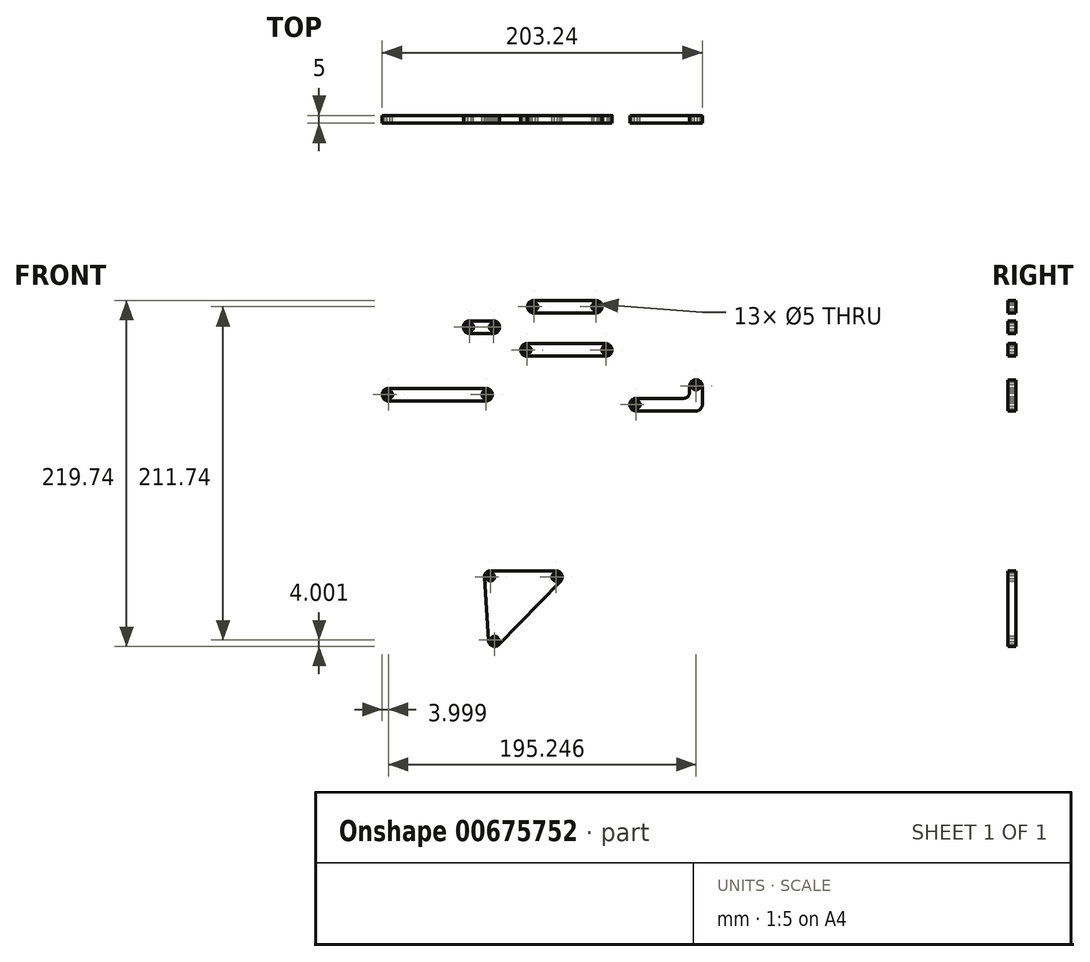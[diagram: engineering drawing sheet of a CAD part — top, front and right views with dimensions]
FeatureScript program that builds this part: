
annotation { "Feature Type Name" : "Feature", "Feature Type Description" : "" }
export const myFeature = defineFeature(function(context is Context, id is Id, definition is map)
    precondition{}
    {
        {
            var Q0;
            Q0=qCreatedBy(makeId("Front.planeOp"),FACE);
            var sketch = newSketch(context, id + "F0", { "sketchPlane" : qUnion([Q0])});
            skLineSegment(sketch, "E0.bottom", {"start": v(-7.5, 4) * mm, "end": v(7.5, 4) * mm});
            skLineSegment(sketch, "E0.top", {"start": v(-7.5, -4) * mm, "end": v(7.5, -4) * mm});
            skLineSegment(sketch, "E0.left", {"start": v(-7.5, 4) * mm, "end": v(-7.5, -4) * mm});
            skLineSegment(sketch, "E0.right", {"start": v(7.5, 4) * mm, "end": v(7.5, -4) * mm});
            skArc(sketch, "E1", {"start": v(7.5, -4) * mm, "mid": v(11.5, 0) * mm, "end": v(7.5, 4) * mm});
            skArc(sketch, "E2", {"start": v(-7.5, 4) * mm, "mid": v(-11.5, 0) * mm, "end": v(-7.5, -4) * mm});
            skCircle(sketch, "E3", {"center": v(-7.5, 0) * mm, "radius": 2.5 * mm});
            skCircle(sketch, "E4", {"center": v(7.5, 0) * mm, "radius": 2.5 * mm});
            skCircle(sketch, "E5", {"center": v(-7.5, 0) * mm, "radius": 1 * mm});
            skCircle(sketch, "E6", {"center": v(7.5, 0) * mm, "radius": 1 * mm});
            skLineSegment(sketch, "E7", {"start": v(-7.5, 0) * mm, "end": v(7.5, 0) * mm});
            skSolve(sketch);
        }
        {
            var Q0;
            {var subQ6=sQuery(id+"F0.wireOp",EDGE,"E0.bottom");Q0=makeQuery(id+"F0.imprint","IMPRINT",FACE,{"disambiguationData":[TD([[makeQuery(id+"F0.imprint","IMPRINT",EDGE,{"derivedFrom":subQ6}),-1.0]])]});}
            var Q1;
            {var subQ5=sQuery(id+"F0.wireOp",EDGE,"E0.top");Q1=makeQuery(id+"F0.imprint","IMPRINT",FACE,{"disambiguationData":[TD([[makeQuery(id+"F0.imprint","IMPRINT",EDGE,{"derivedFrom":subQ5}),1.0]])]});}
            var Q2;
            {var subQ0=sQuery(id+"F0.wireOp",EDGE,"E2");Q2=makeQuery(id+"F0.imprint","IMPRINT",FACE,{"disambiguationData":[TD([[makeQuery(id+"F0.imprint","IMPRINT",EDGE,{"derivedFrom":subQ0}),1.0]])]});}
            var Q3;
            {var subQ0=sQuery(id+"F0.wireOp",EDGE,"E7");var subQ1=sQuery(id+"F0.wireOp",EDGE,"E0.left");var subQ2=makeQuery(id+"F0.imprint","INTERSECT",VERTEX,{"derivedFrom":[subQ1,subQ0]});Q3=makeQuery(id+"F0.imprint","IMPRINT",FACE,{"disambiguationData":[TD([[makeQuery(id+"F0.imprint","IMPRINT",EDGE,{"disambiguationData":[TD([[subQ2,1.0]])],"derivedFrom":subQ1}),1.0]])]});}
            var Q4;
            {var subQ0=sQuery(id+"F0.wireOp",EDGE,"E7");var subQ1=sQuery(id+"F0.wireOp",EDGE,"E0.left");var subQ2=makeQuery(id+"F0.imprint","INTERSECT",VERTEX,{"derivedFrom":[subQ1,subQ0]});Q4=makeQuery(id+"F0.imprint","IMPRINT",FACE,{"disambiguationData":[TD([[makeQuery(id+"F0.imprint","IMPRINT",EDGE,{"disambiguationData":[TD([[subQ2,-1.0]])],"derivedFrom":subQ1}),1.0]])]});}
            var Q5;
            {var subQ0=sQuery(id+"F0.wireOp",EDGE,"E0.left");var subQ1=makeQuery(id+"F0.imprint","INTERSECT",VERTEX,{"derivedFrom":[subQ0,sQuery(id+"F0.wireOp",EDGE,"E7")]});Q5=makeQuery(id+"F0.imprint","IMPRINT",FACE,{"disambiguationData":[TD([[makeQuery(id+"F0.imprint","IMPRINT",EDGE,{"disambiguationData":[TD([[subQ1,1.0]])],"derivedFrom":subQ0}),-1.0]])]});}
            var Q6;
            {var subQ0=sQuery(id+"F0.wireOp",EDGE,"E0.right");var subQ1=makeQuery(id+"F0.imprint","INTERSECT",VERTEX,{"derivedFrom":[subQ0,sQuery(id+"F0.wireOp",EDGE,"E7")]});Q6=makeQuery(id+"F0.imprint","IMPRINT",FACE,{"disambiguationData":[TD([[makeQuery(id+"F0.imprint","IMPRINT",EDGE,{"disambiguationData":[TD([[subQ1,1.0]])],"derivedFrom":subQ0}),1.0]])]});}
            var Q7;
            {var subQ0=sQuery(id+"F0.wireOp",EDGE,"E7");var subQ1=sQuery(id+"F0.wireOp",EDGE,"E0.right");var subQ2=makeQuery(id+"F0.imprint","INTERSECT",VERTEX,{"derivedFrom":[subQ1,subQ0]});Q7=makeQuery(id+"F0.imprint","IMPRINT",FACE,{"disambiguationData":[TD([[makeQuery(id+"F0.imprint","IMPRINT",EDGE,{"disambiguationData":[TD([[subQ2,1.0]])],"derivedFrom":subQ1}),-1.0]])]});}
            var Q8;
            {var subQ0=sQuery(id+"F0.wireOp",EDGE,"E7");var subQ1=sQuery(id+"F0.wireOp",EDGE,"E0.right");var subQ2=makeQuery(id+"F0.imprint","INTERSECT",VERTEX,{"derivedFrom":[subQ1,subQ0]});Q8=makeQuery(id+"F0.imprint","IMPRINT",FACE,{"disambiguationData":[TD([[makeQuery(id+"F0.imprint","IMPRINT",EDGE,{"disambiguationData":[TD([[subQ2,-1.0]])],"derivedFrom":subQ1}),-1.0]])]});}
            var Q9;
            {var subQ0=sQuery(id+"F0.wireOp",EDGE,"E1");Q9=makeQuery(id+"F0.imprint","IMPRINT",FACE,{"disambiguationData":[TD([[makeQuery(id+"F0.imprint","IMPRINT",EDGE,{"derivedFrom":subQ0}),1.0]])]});}
            extrude(context, id + "F1", {"entities" : qUnion([Q0, Q1, Q2, Q3, Q4, Q5, Q6, Q7, Q8, Q9]), "endBound" : BoundingType.SYMMETRIC, "depth" : 5 * mm, "offsetDistance" : 25 * mm});
        }
        {
            var Q0;
            Q0=qCreatedBy(makeId("Front.planeOp"),FACE);
            var sketch = newSketch(context, id + "F2", { "sketchPlane" : qUnion([Q0])});
            skLineSegment(sketch, "E8.bottom", {"start": v(33.28, 16.95) * mm, "end": v(72.58, 16.95) * mm});
            skLineSegment(sketch, "E8.top", {"start": v(33.28, 8.95) * mm, "end": v(72.58, 8.95) * mm});
            skLineSegment(sketch, "E8.left", {"start": v(33.28, 16.95) * mm, "end": v(33.28, 8.95) * mm});
            skLineSegment(sketch, "E8.right", {"start": v(72.58, 16.95) * mm, "end": v(72.58, 8.95) * mm});
            skArc(sketch, "E9", {"start": v(33.28, 16.95) * mm, "mid": v(29.28, 12.95) * mm, "end": v(33.28, 8.95) * mm});
            skArc(sketch, "E10", {"start": v(72.58, 8.95) * mm, "mid": v(76.58, 12.95) * mm, "end": v(72.58, 16.95) * mm});
            skCircle(sketch, "E11", {"center": v(33.28, 12.95) * mm, "radius": 2.5 * mm});
            skCircle(sketch, "E12", {"center": v(33.28, 12.95) * mm, "radius": 1 * mm});
            skCircle(sketch, "E13", {"center": v(72.58, 12.95) * mm, "radius": 2.5 * mm});
            skCircle(sketch, "E14", {"center": v(72.58, 12.95) * mm, "radius": 1 * mm});
            skSolve(sketch);
        }
        {
            var Q0;
            {var subQ2=sQuery(id+"F2.wireOp",EDGE,"E8.bottom");Q0=makeQuery(id+"F2.imprint","IMPRINT",FACE,{"disambiguationData":[TD([[makeQuery(id+"F2.imprint","IMPRINT",EDGE,{"derivedFrom":subQ2}),-1.0]])]});}
            var Q1;
            {var subQ0=sQuery(id+"F2.wireOp",EDGE,"E9");Q1=makeQuery(id+"F2.imprint","IMPRINT",FACE,{"disambiguationData":[TD([[makeQuery(id+"F2.imprint","IMPRINT",EDGE,{"derivedFrom":subQ0}),1.0]])]});}
            var Q2;
            {var subQ0=sQuery(id+"F2.wireOp",EDGE,"E10");Q2=makeQuery(id+"F2.imprint","IMPRINT",FACE,{"disambiguationData":[TD([[makeQuery(id+"F2.imprint","IMPRINT",EDGE,{"derivedFrom":subQ0}),1.0]])]});}
            var Q3;
            {var subQ0=sQuery(id+"F2.wireOp",EDGE,"E14");var subQ1=sQuery(id+"F2.wireOp",EDGE,"E8.right");var subQ2=makeQuery(id+"F2.imprint","INTERSECT",VERTEX,{"disambiguationData":[OD(0.0)],"derivedFrom":[subQ1,subQ0]});Q3=makeQuery(id+"F2.imprint","IMPRINT",FACE,{"disambiguationData":[TD([[makeQuery(id+"F2.imprint","IMPRINT",EDGE,{"disambiguationData":[TD([[subQ2,-1.0]])],"derivedFrom":subQ1}),1.0]])]});}
            var Q4;
            {var subQ0=sQuery(id+"F2.wireOp",EDGE,"E14");var subQ1=sQuery(id+"F2.wireOp",EDGE,"E8.right");var subQ2=makeQuery(id+"F2.imprint","INTERSECT",VERTEX,{"disambiguationData":[OD(0.0)],"derivedFrom":[subQ1,subQ0]});Q4=makeQuery(id+"F2.imprint","IMPRINT",FACE,{"disambiguationData":[TD([[makeQuery(id+"F2.imprint","IMPRINT",EDGE,{"disambiguationData":[TD([[subQ2,-1.0]])],"derivedFrom":subQ1}),-1.0]])]});}
            var Q5;
            {var subQ0=sQuery(id+"F2.wireOp",EDGE,"E12");var subQ1=sQuery(id+"F2.wireOp",EDGE,"E8.left");var subQ2=makeQuery(id+"F2.imprint","INTERSECT",VERTEX,{"disambiguationData":[OD(0.0)],"derivedFrom":[subQ1,subQ0]});Q5=makeQuery(id+"F2.imprint","IMPRINT",FACE,{"disambiguationData":[TD([[makeQuery(id+"F2.imprint","IMPRINT",EDGE,{"disambiguationData":[TD([[subQ2,-1.0]])],"derivedFrom":subQ1}),1.0]])]});}
            var Q6;
            {var subQ0=sQuery(id+"F2.wireOp",EDGE,"E12");var subQ1=sQuery(id+"F2.wireOp",EDGE,"E8.left");var subQ2=makeQuery(id+"F2.imprint","INTERSECT",VERTEX,{"disambiguationData":[OD(0.0)],"derivedFrom":[subQ1,subQ0]});Q6=makeQuery(id+"F2.imprint","IMPRINT",FACE,{"disambiguationData":[TD([[makeQuery(id+"F2.imprint","IMPRINT",EDGE,{"disambiguationData":[TD([[subQ2,-1.0]])],"derivedFrom":subQ1}),-1.0]])]});}
            extrude(context, id + "F3", {"entities" : qUnion([Q0, Q1, Q2, Q3, Q4, Q5, Q6]), "endBound" : BoundingType.SYMMETRIC, "depth" : 5 * mm, "offsetDistance" : 25 * mm});
        }
        {
            var Q0;
            Q0=qCreatedBy(makeId("Front.planeOp"),FACE);
            var sketch = newSketch(context, id + "F4", { "sketchPlane" : qUnion([Q0])});
            skLineSegment(sketch, "E15.bottom", {"start": v(28.9, -10.5) * mm, "end": v(78.9, -10.5) * mm});
            skLineSegment(sketch, "E15.top", {"start": v(28.9, -18.5) * mm, "end": v(78.9, -18.5) * mm});
            skLineSegment(sketch, "E15.left", {"start": v(28.9, -10.5) * mm, "end": v(28.9, -18.5) * mm});
            skLineSegment(sketch, "E15.right", {"start": v(78.9, -10.5) * mm, "end": v(78.9, -18.5) * mm});
            skArc(sketch, "E16", {"start": v(28.9, -10.5) * mm, "mid": v(24.9, -14.5) * mm, "end": v(28.9, -18.5) * mm});
            skArc(sketch, "E17", {"start": v(78.9, -18.5) * mm, "mid": v(82.9, -14.5) * mm, "end": v(78.9, -10.5) * mm});
            skCircle(sketch, "E18", {"center": v(28.9, -14.5) * mm, "radius": 2.5 * mm});
            skCircle(sketch, "E19", {"center": v(28.9, -14.5) * mm, "radius": 1 * mm});
            skCircle(sketch, "E20", {"center": v(78.9, -14.5) * mm, "radius": 2.5 * mm});
            skCircle(sketch, "E21", {"center": v(78.9, -14.5) * mm, "radius": 1 * mm});
            skSolve(sketch);
        }
        {
            var Q0;
            {var subQ2=sQuery(id+"F4.wireOp",EDGE,"E15.bottom");Q0=makeQuery(id+"F4.imprint","IMPRINT",FACE,{"disambiguationData":[TD([[makeQuery(id+"F4.imprint","IMPRINT",EDGE,{"derivedFrom":subQ2}),-1.0]])]});}
            var Q1;
            {var subQ0=sQuery(id+"F4.wireOp",EDGE,"E16");Q1=makeQuery(id+"F4.imprint","IMPRINT",FACE,{"disambiguationData":[TD([[makeQuery(id+"F4.imprint","IMPRINT",EDGE,{"derivedFrom":subQ0}),1.0]])]});}
            var Q2;
            {var subQ0=sQuery(id+"F4.wireOp",EDGE,"E17");Q2=makeQuery(id+"F4.imprint","IMPRINT",FACE,{"disambiguationData":[TD([[makeQuery(id+"F4.imprint","IMPRINT",EDGE,{"derivedFrom":subQ0}),1.0]])]});}
            var Q3;
            {var subQ0=sQuery(id+"F4.wireOp",EDGE,"E21");var subQ1=sQuery(id+"F4.wireOp",EDGE,"E15.right");var subQ2=makeQuery(id+"F4.imprint","INTERSECT",VERTEX,{"disambiguationData":[OD(0.0)],"derivedFrom":[subQ1,subQ0]});Q3=makeQuery(id+"F4.imprint","IMPRINT",FACE,{"disambiguationData":[TD([[makeQuery(id+"F4.imprint","IMPRINT",EDGE,{"disambiguationData":[TD([[subQ2,-1.0]])],"derivedFrom":subQ1}),1.0]])]});}
            var Q4;
            {var subQ0=sQuery(id+"F4.wireOp",EDGE,"E21");var subQ1=sQuery(id+"F4.wireOp",EDGE,"E15.right");var subQ2=makeQuery(id+"F4.imprint","INTERSECT",VERTEX,{"disambiguationData":[OD(0.0)],"derivedFrom":[subQ1,subQ0]});Q4=makeQuery(id+"F4.imprint","IMPRINT",FACE,{"disambiguationData":[TD([[makeQuery(id+"F4.imprint","IMPRINT",EDGE,{"disambiguationData":[TD([[subQ2,-1.0]])],"derivedFrom":subQ1}),-1.0]])]});}
            var Q5;
            {var subQ0=sQuery(id+"F4.wireOp",EDGE,"E19");var subQ1=sQuery(id+"F4.wireOp",EDGE,"E15.left");var subQ2=makeQuery(id+"F4.imprint","INTERSECT",VERTEX,{"disambiguationData":[OD(0.0)],"derivedFrom":[subQ1,subQ0]});Q5=makeQuery(id+"F4.imprint","IMPRINT",FACE,{"disambiguationData":[TD([[makeQuery(id+"F4.imprint","IMPRINT",EDGE,{"disambiguationData":[TD([[subQ2,-1.0]])],"derivedFrom":subQ1}),1.0]])]});}
            var Q6;
            {var subQ0=sQuery(id+"F4.wireOp",EDGE,"E19");var subQ1=sQuery(id+"F4.wireOp",EDGE,"E15.left");var subQ2=makeQuery(id+"F4.imprint","INTERSECT",VERTEX,{"disambiguationData":[OD(0.0)],"derivedFrom":[subQ1,subQ0]});Q6=makeQuery(id+"F4.imprint","IMPRINT",FACE,{"disambiguationData":[TD([[makeQuery(id+"F4.imprint","IMPRINT",EDGE,{"disambiguationData":[TD([[subQ2,-1.0]])],"derivedFrom":subQ1}),-1.0]])]});}
            extrude(context, id + "F5", {"entities" : qUnion([Q0, Q1, Q2, Q3, Q4, Q5, Q6]), "endBound" : BoundingType.SYMMETRIC, "depth" : 5 * mm, "offsetDistance" : 25 * mm});
        }
        {
            var Q0;
            Q0=qCreatedBy(makeId("Front.planeOp"),FACE);
            var sketch = newSketch(context, id + "F6", { "sketchPlane" : qUnion([Q0])});
            skLineSegment(sketch, "E22.bottom", {"start": v(-59.03, -46.94) * mm, "end": v(2.87, -46.94) * mm});
            skLineSegment(sketch, "E22.top", {"start": v(-59.03, -38.94) * mm, "end": v(2.87, -38.94) * mm});
            skLineSegment(sketch, "E22.left", {"start": v(-59.03, -46.94) * mm, "end": v(-59.03, -38.94) * mm});
            skLineSegment(sketch, "E22.right", {"start": v(2.87, -46.94) * mm, "end": v(2.87, -38.94) * mm});
            skArc(sketch, "E23", {"start": v(-59.03, -38.94) * mm, "mid": v(-63.03, -42.94) * mm, "end": v(-59.03, -46.94) * mm});
            skArc(sketch, "E24", {"start": v(2.87, -46.94) * mm, "mid": v(6.87, -42.94) * mm, "end": v(2.87, -38.94) * mm});
            skCircle(sketch, "E25", {"center": v(-59.03, -42.94) * mm, "radius": 2.5 * mm});
            skCircle(sketch, "E26", {"center": v(2.87, -42.94) * mm, "radius": 2.5 * mm});
            skCircle(sketch, "E27", {"center": v(2.87, -42.94) * mm, "radius": 1 * mm});
            skCircle(sketch, "E28", {"center": v(-59.03, -42.94) * mm, "radius": 1 * mm});
            skSolve(sketch);
        }
        {
            var Q0;
            {var subQ2=sQuery(id+"F6.wireOp",EDGE,"E22.bottom");Q0=makeQuery(id+"F6.imprint","IMPRINT",FACE,{"disambiguationData":[TD([[makeQuery(id+"F6.imprint","IMPRINT",EDGE,{"derivedFrom":subQ2}),1.0]])]});}
            var Q1;
            {var subQ0=sQuery(id+"F6.wireOp",EDGE,"E23");Q1=makeQuery(id+"F6.imprint","IMPRINT",FACE,{"disambiguationData":[TD([[makeQuery(id+"F6.imprint","IMPRINT",EDGE,{"derivedFrom":subQ0}),1.0]])]});}
            var Q2;
            {var subQ0=sQuery(id+"F6.wireOp",EDGE,"E28");var subQ1=sQuery(id+"F6.wireOp",EDGE,"E22.left");var subQ2=makeQuery(id+"F6.imprint","INTERSECT",VERTEX,{"disambiguationData":[OD(0.0)],"derivedFrom":[subQ1,subQ0]});Q2=makeQuery(id+"F6.imprint","IMPRINT",FACE,{"disambiguationData":[TD([[makeQuery(id+"F6.imprint","IMPRINT",EDGE,{"disambiguationData":[TD([[subQ2,-1.0]])],"derivedFrom":subQ1}),-1.0]])]});}
            var Q3;
            {var subQ0=sQuery(id+"F6.wireOp",EDGE,"E28");var subQ1=sQuery(id+"F6.wireOp",EDGE,"E22.left");var subQ2=makeQuery(id+"F6.imprint","INTERSECT",VERTEX,{"disambiguationData":[OD(0.0)],"derivedFrom":[subQ1,subQ0]});Q3=makeQuery(id+"F6.imprint","IMPRINT",FACE,{"disambiguationData":[TD([[makeQuery(id+"F6.imprint","IMPRINT",EDGE,{"disambiguationData":[TD([[subQ2,-1.0]])],"derivedFrom":subQ1}),1.0]])]});}
            var Q4;
            {var subQ0=sQuery(id+"F6.wireOp",EDGE,"E24");Q4=makeQuery(id+"F6.imprint","IMPRINT",FACE,{"disambiguationData":[TD([[makeQuery(id+"F6.imprint","IMPRINT",EDGE,{"derivedFrom":subQ0}),1.0]])]});}
            var Q5;
            {var subQ0=sQuery(id+"F6.wireOp",EDGE,"E27");var subQ1=sQuery(id+"F6.wireOp",EDGE,"E22.right");var subQ2=makeQuery(id+"F6.imprint","INTERSECT",VERTEX,{"disambiguationData":[OD(0.0)],"derivedFrom":[subQ1,subQ0]});Q5=makeQuery(id+"F6.imprint","IMPRINT",FACE,{"disambiguationData":[TD([[makeQuery(id+"F6.imprint","IMPRINT",EDGE,{"disambiguationData":[TD([[subQ2,-1.0]])],"derivedFrom":subQ1}),-1.0]])]});}
            var Q6;
            {var subQ0=sQuery(id+"F6.wireOp",EDGE,"E27");var subQ1=sQuery(id+"F6.wireOp",EDGE,"E22.right");var subQ2=makeQuery(id+"F6.imprint","INTERSECT",VERTEX,{"disambiguationData":[OD(0.0)],"derivedFrom":[subQ1,subQ0]});Q6=makeQuery(id+"F6.imprint","IMPRINT",FACE,{"disambiguationData":[TD([[makeQuery(id+"F6.imprint","IMPRINT",EDGE,{"disambiguationData":[TD([[subQ2,-1.0]])],"derivedFrom":subQ1}),1.0]])]});}
            extrude(context, id + "F7", {"entities" : qUnion([Q0, Q1, Q2, Q3, Q4, Q5, Q6]), "endBound" : BoundingType.SYMMETRIC, "depth" : 5 * mm, "offsetDistance" : 25 * mm});
        }
        {
            var Q0;
            Q0=qCreatedBy(makeId("Front.planeOp"),FACE);
            var sketch = newSketch(context, id + "F8", { "sketchPlane" : qUnion([Q0])});
            skLineSegment(sketch, "E29.bottom", {"start": v(98.21, -45.24) * mm, "end": v(128.21, -45.24) * mm});
            skLineSegment(sketch, "E29.top", {"start": v(98.21, -53.24) * mm, "end": v(136.21, -53.24) * mm});
            skLineSegment(sketch, "E29.left", {"start": v(98.21, -45.24) * mm, "end": v(98.21, -53.24) * mm});
            skLineSegment(sketch, "E29.right", {"start": v(140.21, -45.24) * mm, "end": v(140.21, -49.24) * mm});
            skArc(sketch, "E30", {"start": v(98.21, -45.24) * mm, "mid": v(94.21, -49.24) * mm, "end": v(98.21, -53.24) * mm});
            skLineSegment(sketch, "E31.top", {"start": v(140.21, -37.44) * mm, "end": v(132.21, -37.44) * mm});
            skLineSegment(sketch, "E31.left", {"start": v(140.21, -45.24) * mm, "end": v(140.21, -37.44) * mm});
            skLineSegment(sketch, "E31.right", {"start": v(132.21, -41.24) * mm, "end": v(132.21, -37.44) * mm});
            skArc(sketch, "E32", {"start": v(140.21, -37.44) * mm, "mid": v(136.21, -33.44) * mm, "end": v(132.21, -37.44) * mm});
            skPoint(sketch, "E33.visualSharp", {"position": v(132.21, -45.24) * mm});
            skArc(sketch, "E33.filletArc", {"start": v(128.21, -45.24) * mm, "mid": v(131.04, -44.07) * mm, "end": v(132.21, -41.24) * mm});
            skCircle(sketch, "E34", {"center": v(98.21, -49.24) * mm, "radius": 2.5 * mm});
            skCircle(sketch, "E35", {"center": v(98.21, -49.24) * mm, "radius": 1 * mm});
            skCircle(sketch, "E36", {"center": v(136.21, -37.44) * mm, "radius": 2.5 * mm});
            skCircle(sketch, "E37", {"center": v(136.21, -37.44) * mm, "radius": 1 * mm});
            skPoint(sketch, "E38.visualSharp", {"position": v(140.21, -53.24) * mm});
            skArc(sketch, "E38.filletArc", {"start": v(136.21, -53.24) * mm, "mid": v(139.04, -52.07) * mm, "end": v(140.21, -49.24) * mm});
            skSolve(sketch);
        }
        {
            var Q0;
            {var subQ6=sQuery(id+"F8.wireOp",EDGE,"E29.bottom");Q0=makeQuery(id+"F8.imprint","IMPRINT",FACE,{"disambiguationData":[TD([[makeQuery(id+"F8.imprint","IMPRINT",EDGE,{"derivedFrom":subQ6}),-1.0]])]});}
            var Q1;
            {var subQ0=sQuery(id+"F8.wireOp",EDGE,"E30");Q1=makeQuery(id+"F8.imprint","IMPRINT",FACE,{"disambiguationData":[TD([[makeQuery(id+"F8.imprint","IMPRINT",EDGE,{"derivedFrom":subQ0}),1.0]])]});}
            var Q2;
            {var subQ0=sQuery(id+"F8.wireOp",EDGE,"E35");var subQ1=sQuery(id+"F8.wireOp",EDGE,"E29.left");var subQ2=makeQuery(id+"F8.imprint","INTERSECT",VERTEX,{"disambiguationData":[OD(0.0)],"derivedFrom":[subQ1,subQ0]});Q2=makeQuery(id+"F8.imprint","IMPRINT",FACE,{"disambiguationData":[TD([[makeQuery(id+"F8.imprint","IMPRINT",EDGE,{"disambiguationData":[TD([[subQ2,-1.0]])],"derivedFrom":subQ1}),1.0]])]});}
            var Q3;
            {var subQ0=sQuery(id+"F8.wireOp",EDGE,"E35");var subQ1=sQuery(id+"F8.wireOp",EDGE,"E29.left");var subQ2=makeQuery(id+"F8.imprint","INTERSECT",VERTEX,{"disambiguationData":[OD(0.0)],"derivedFrom":[subQ1,subQ0]});Q3=makeQuery(id+"F8.imprint","IMPRINT",FACE,{"disambiguationData":[TD([[makeQuery(id+"F8.imprint","IMPRINT",EDGE,{"disambiguationData":[TD([[subQ2,-1.0]])],"derivedFrom":subQ1}),-1.0]])]});}
            var Q4;
            {var subQ0=sQuery(id+"F8.wireOp",EDGE,"E32");Q4=makeQuery(id+"F8.imprint","IMPRINT",FACE,{"disambiguationData":[TD([[makeQuery(id+"F8.imprint","IMPRINT",EDGE,{"derivedFrom":subQ0}),1.0]])]});}
            var Q5;
            {var subQ0=sQuery(id+"F8.wireOp",EDGE,"E37");var subQ1=sQuery(id+"F8.wireOp",EDGE,"E31.top");var subQ2=makeQuery(id+"F8.imprint","INTERSECT",VERTEX,{"disambiguationData":[OD(0.0)],"derivedFrom":[subQ1,subQ0]});Q5=makeQuery(id+"F8.imprint","IMPRINT",FACE,{"disambiguationData":[TD([[makeQuery(id+"F8.imprint","IMPRINT",EDGE,{"disambiguationData":[TD([[subQ2,-1.0]])],"derivedFrom":subQ1}),-1.0]])]});}
            var Q6;
            {var subQ0=sQuery(id+"F8.wireOp",EDGE,"E37");var subQ1=sQuery(id+"F8.wireOp",EDGE,"E31.top");var subQ2=makeQuery(id+"F8.imprint","INTERSECT",VERTEX,{"disambiguationData":[OD(0.0)],"derivedFrom":[subQ1,subQ0]});Q6=makeQuery(id+"F8.imprint","IMPRINT",FACE,{"disambiguationData":[TD([[makeQuery(id+"F8.imprint","IMPRINT",EDGE,{"disambiguationData":[TD([[subQ2,-1.0]])],"derivedFrom":subQ1}),1.0]])]});}
            extrude(context, id + "F9", {"entities" : qUnion([Q0, Q1, Q2, Q3, Q4, Q5, Q6]), "endBound" : BoundingType.SYMMETRIC, "depth" : 5 * mm, "offsetDistance" : 25 * mm});
        }
        {
            var Q0;
            Q0=qCreatedBy(makeId("Front.planeOp"),FACE);
            var sketch = newSketch(context, id + "F10", { "sketchPlane" : qUnion([Q0])});
            skLineSegment(sketch, "E39", {"start": v(5.76, -158.77) * mm, "end": v(47.26, -158.77) * mm});
            skLineSegment(sketch, "E40", {"start": v(47.26, -158.77) * mm, "end": v(8.37, -198.79) * mm});
            skLineSegment(sketch, "E41", {"start": v(8.37, -198.79) * mm, "end": v(5.76, -158.77) * mm});
            skArc(sketch, "E42", {"start": v(5.76, -154.77) * mm, "mid": v(2.84, -156.04) * mm, "end": v(1.77, -159.03) * mm});
            skArc(sketch, "E43", {"start": v(50.13, -161.56) * mm, "mid": v(50.95, -157.22) * mm, "end": v(47.26, -154.77) * mm});
            skArc(sketch, "E44", {"start": v(4.38, -199.05) * mm, "mid": v(7, -202.54) * mm, "end": v(11.24, -201.58) * mm});
            skLineSegment(sketch, "E45", {"start": v(1.77, -159.03) * mm, "end": v(4.38, -199.05) * mm});
            skLineSegment(sketch, "E46", {"start": v(11.24, -201.58) * mm, "end": v(50.13, -161.56) * mm});
            skLineSegment(sketch, "E47", {"start": v(5.76, -154.77) * mm, "end": v(47.26, -154.77) * mm});
            skCircle(sketch, "E48", {"center": v(5.76, -158.77) * mm, "radius": 2.5 * mm});
            skCircle(sketch, "E49", {"center": v(5.76, -158.77) * mm, "radius": 1 * mm});
            skCircle(sketch, "E50", {"center": v(47.26, -158.77) * mm, "radius": 2.5 * mm});
            skCircle(sketch, "E51", {"center": v(47.26, -158.77) * mm, "radius": 1 * mm});
            skCircle(sketch, "E52", {"center": v(8.37, -198.79) * mm, "radius": 2.5 * mm});
            skCircle(sketch, "E53", {"center": v(8.37, -198.79) * mm, "radius": 1 * mm});
            skSolve(sketch);
        }
        {
            var Q0;
            Q0=makeQuery(id+"F10.imprint","IMPRINT",FACE,{"disambiguationData":[TD([[makeQuery(id+"F10.imprint","IMPRINT",EDGE,{"derivedFrom":sQuery(id+"F10.wireOp",EDGE,"E42")}),1.0]])]});
            var Q1;
            {var subQ0=sQuery(id+"F10.wireOp",EDGE,"E48");var subQ1=sQuery(id+"F10.wireOp",EDGE,"E39");var subQ2=makeQuery(id+"F10.imprint","INTERSECT",VERTEX,{"derivedFrom":[subQ1,subQ0]});Q1=makeQuery(id+"F10.imprint","IMPRINT",FACE,{"disambiguationData":[TD([[makeQuery(id+"F10.imprint","IMPRINT",EDGE,{"disambiguationData":[TD([[subQ2,-1.0]])],"derivedFrom":subQ1}),-1.0]])]});}
            var Q2;
            {var subQ0=sQuery(id+"F10.wireOp",EDGE,"E41");var subQ1=sQuery(id+"F10.wireOp",EDGE,"E40");var subQ2=makeQuery(id+"F10.imprint","INTERSECT",VERTEX,{"derivedFrom":[subQ1,subQ0]});Q2=makeQuery(id+"F10.imprint","IMPRINT",FACE,{"disambiguationData":[TD([[makeQuery(id+"F10.imprint","IMPRINT",EDGE,{"disambiguationData":[TD([[subQ2,1.0]])],"derivedFrom":subQ1}),-1.0]])]});}
            var Q3;
            {var subQ0=sQuery(id+"F10.wireOp",EDGE,"E41");var subQ1=sQuery(id+"F10.wireOp",EDGE,"E40");var subQ2=makeQuery(id+"F10.imprint","INTERSECT",VERTEX,{"derivedFrom":[subQ1,subQ0]});Q3=makeQuery(id+"F10.imprint","IMPRINT",FACE,{"disambiguationData":[TD([[makeQuery(id+"F10.imprint","IMPRINT",EDGE,{"disambiguationData":[TD([[subQ2,1.0]])],"derivedFrom":subQ1}),1.0]])]});}
            var Q4;
            {var subQ0=sQuery(id+"F10.wireOp",EDGE,"E41");var subQ1=sQuery(id+"F10.wireOp",EDGE,"E39");var subQ2=makeQuery(id+"F10.imprint","INTERSECT",VERTEX,{"derivedFrom":[subQ1,subQ0]});Q4=makeQuery(id+"F10.imprint","IMPRINT",FACE,{"disambiguationData":[TD([[makeQuery(id+"F10.imprint","IMPRINT",EDGE,{"disambiguationData":[TD([[subQ2,-1.0]])],"derivedFrom":subQ1}),-1.0]])]});}
            var Q5;
            {var subQ0=sQuery(id+"F10.wireOp",EDGE,"E41");var subQ1=sQuery(id+"F10.wireOp",EDGE,"E39");var subQ2=makeQuery(id+"F10.imprint","INTERSECT",VERTEX,{"derivedFrom":[subQ1,subQ0]});Q5=makeQuery(id+"F10.imprint","IMPRINT",FACE,{"disambiguationData":[TD([[makeQuery(id+"F10.imprint","IMPRINT",EDGE,{"disambiguationData":[TD([[subQ2,-1.0]])],"derivedFrom":subQ1}),1.0]])]});}
            var Q6;
            {var subQ0=sQuery(id+"F10.wireOp",EDGE,"E40");var subQ1=sQuery(id+"F10.wireOp",EDGE,"E39");var subQ2=makeQuery(id+"F10.imprint","INTERSECT",VERTEX,{"derivedFrom":[subQ1,subQ0]});Q6=makeQuery(id+"F10.imprint","IMPRINT",FACE,{"disambiguationData":[TD([[makeQuery(id+"F10.imprint","IMPRINT",EDGE,{"disambiguationData":[TD([[subQ2,1.0]])],"derivedFrom":subQ1}),1.0]])]});}
            var Q7;
            {var subQ0=sQuery(id+"F10.wireOp",EDGE,"E40");var subQ1=sQuery(id+"F10.wireOp",EDGE,"E39");var subQ2=makeQuery(id+"F10.imprint","INTERSECT",VERTEX,{"derivedFrom":[subQ1,subQ0]});Q7=makeQuery(id+"F10.imprint","IMPRINT",FACE,{"disambiguationData":[TD([[makeQuery(id+"F10.imprint","IMPRINT",EDGE,{"disambiguationData":[TD([[subQ2,1.0]])],"derivedFrom":subQ1}),-1.0]])]});}
            extrude(context, id + "F11", {"entities" : qUnion([Q0, Q1, Q2, Q3, Q4, Q5, Q6, Q7]), "endBound" : BoundingType.SYMMETRIC, "depth" : 5 * mm, "offsetDistance" : 25 * mm});
        }
    });
